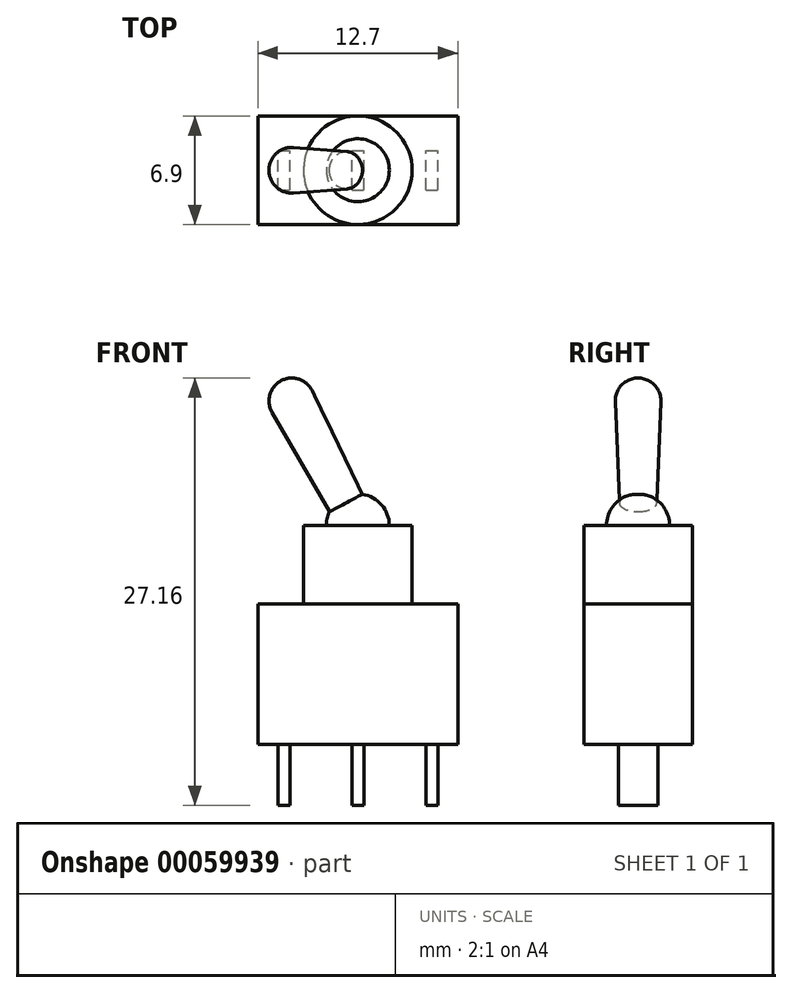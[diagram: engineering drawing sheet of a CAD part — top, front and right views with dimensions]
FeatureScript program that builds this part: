
annotation { "Feature Type Name" : "Feature", "Feature Type Description" : "" }
export const myFeature = defineFeature(function(context is Context, id is Id, definition is map)
    precondition{}
    {
        {
            var Q0;
            Q0=qCreatedBy(makeId("Top.planeOp"),FACE);
            var sketch = newSketch(context, id + "F0", { "sketchPlane" : qUnion([Q0])});
            skLineSegment(sketch, "E0.bottom", {"start": v(0, -3.45) * mm, "end": v(12.7, -3.45) * mm});
            skLineSegment(sketch, "E0.top", {"start": v(0, 3.45) * mm, "end": v(12.7, 3.45) * mm});
            skLineSegment(sketch, "E0.left", {"start": v(0, -3.45) * mm, "end": v(0, 3.45) * mm});
            skLineSegment(sketch, "E0.right", {"start": v(12.7, -3.45) * mm, "end": v(12.7, 3.45) * mm});
            skSolve(sketch);
        }
        {
            var Q0;
            Q0=makeQuery(id+"F0.imprint","IMPRINT",FACE,{"disambiguationData":[TD([[makeQuery(id+"F0.imprint","IMPRINT",EDGE,{"derivedFrom":sQuery(id+"F0.wireOp",EDGE,"E0.bottom")}),1.0]])]});
            extrude(context, id + "F1", {"entities" : qUnion([Q0]), "depth" : 8.9 * mm});
        }
        {
            var Q0;
            Q0=makeQuery(id+"F1.opExtrude","CAP_FACE",FACE,{"disambiguationData":[OSD([sQuery(id+"F0.wireOp",EDGE,"E0.bottom"),sQuery(id+"F0.wireOp",EDGE,"E0.top"),sQuery(id+"F0.wireOp",EDGE,"E0.left"),sQuery(id+"F0.wireOp",EDGE,"E0.right")])],"isStart":false});
            var sketch = newSketch(context, id + "F2", { "sketchPlane" : qUnion([Q0])});
            skCircle(sketch, "E1", {"center": v(6.35, 0) * mm, "radius": 3.45 * mm});
            skLineSegment(sketch, "E2", {"start": v(0, 0) * mm, "end": v(6.35, 0) * mm, "construction": true});
            skLineSegment(sketch, "E3", {"start": v(6.35, -3.45) * mm, "end": v(6.35, 3.45) * mm, "construction": true});
            skSolve(sketch);
        }
        {
            var Q0;
            Q0=makeQuery(id+"F2.imprint","IMPRINT",FACE,{"disambiguationData":[TD([[makeQuery(id+"F2.imprint","IMPRINT",EDGE,{"derivedFrom":sQuery(id+"F2.wireOp",EDGE,"E1")}),1.0]])]});
            extrude(context, id + "F3", {"entities" : qUnion([Q0]), "operationType" : NewBodyOperationType.ADD, "depth" : 5 * mm});
        }
        {
            var Q0;
            Q0=qCreatedBy(makeId("Front.planeOp"),FACE);
            var sketch = newSketch(context, id + "F4", { "sketchPlane" : qUnion([Q0])});
            skLineSegment(sketch, "E4", {"start": v(5.05, 13.9) * mm, "end": v(0.9, 21.08) * mm});
            skLineSegment(sketch, "E5", {"start": v(1.48, 23.09) * mm, "end": v(6.35, 13.9) * mm});
            skArc(sketch, "E6", {"start": v(1.48, 23.09) * mm, "mid": v(0.77, 22.2) * mm, "end": v(0.9, 21.08) * mm});
            skLineSegment(sketch, "E7", {"start": v(5.05, 13.9) * mm, "end": v(6.35, 13.9) * mm});
            skLineSegment(sketch, "E8", {"start": v(5.05, 13.9) * mm, "end": v(20.9, -13.56) * mm, "construction": true});
            skLineSegment(sketch, "E9", {"start": v(20.9, -13.56) * mm, "end": v(6.35, 13.9) * mm, "construction": true});
            skSolve(sketch);
        }
        {
            var Q0;
            Q0=makeQuery(id+"F4.imprint","IMPRINT",FACE,{"disambiguationData":[TD([[makeQuery(id+"F4.imprint","IMPRINT",EDGE,{"derivedFrom":sQuery(id+"F4.wireOp",EDGE,"E4")}),-1.0]])]});
            var Q1;
            Q1=sQuery(id+"F4.wireOp",EDGE,"E5");
            revolve(context, id + "F5", {"operationType" : NewBodyOperationType.ADD, "entities" : qUnion([Q0]), "axis" : qUnion([Q1]), "revolveType" : RevolveType.FULL});
        }
        {
            var Q0;
            Q0=qCreatedBy(makeId("Front.planeOp"),FACE);
            var sketch = newSketch(context, id + "F6", { "sketchPlane" : qUnion([Q0])});
            skLineSegment(sketch, "E10", {"start": v(4.35, 13.9) * mm, "end": v(8.35, 13.9) * mm});
            skArc(sketch, "E11", {"start": v(8.35, 13.9) * mm, "mid": v(6.35, 15.9) * mm, "end": v(4.35, 13.9) * mm});
            skSolve(sketch);
        }
        {
            var Q0;
            Q0 = qSketchRegion(id + "F6", true);
            var Q1;
            Q1=sQuery(id+"F6.wireOp",EDGE,"E10");
            revolve(context, id + "F7", {"operationType" : NewBodyOperationType.ADD, "entities" : qUnion([Q0]), "axis" : qUnion([Q1]), "revolveType" : RevolveType.FULL});
        }
        {
            var Q0;
            Q0=qCreatedBy(makeId("Top.planeOp"),FACE);
            var sketch = newSketch(context, id + "F8", { "sketchPlane" : qUnion([Q0])});
            skLineSegment(sketch, "E12.bottom", {"start": v(1.27, -1.25) * mm, "end": v(2.03, -1.25) * mm});
            skLineSegment(sketch, "E12.top", {"start": v(1.27, 1.25) * mm, "end": v(2.03, 1.25) * mm});
            skLineSegment(sketch, "E12.left", {"start": v(1.27, -1.25) * mm, "end": v(1.27, 1.25) * mm});
            skLineSegment(sketch, "E12.right", {"start": v(2.03, -1.25) * mm, "end": v(2.03, 1.25) * mm});
            skLineSegment(sketch, "E13.bottom", {"start": v(5.97, -1.25) * mm, "end": v(6.73, -1.25) * mm});
            skLineSegment(sketch, "E13.top", {"start": v(5.97, 1.25) * mm, "end": v(6.73, 1.25) * mm});
            skLineSegment(sketch, "E13.left", {"start": v(5.97, -1.25) * mm, "end": v(5.97, 1.25) * mm});
            skLineSegment(sketch, "E13.right", {"start": v(6.73, -1.25) * mm, "end": v(6.73, 1.25) * mm});
            skLineSegment(sketch, "E14.bottom", {"start": v(10.67, -1.25) * mm, "end": v(11.43, -1.25) * mm});
            skLineSegment(sketch, "E14.top", {"start": v(10.67, 1.25) * mm, "end": v(11.43, 1.25) * mm});
            skLineSegment(sketch, "E14.left", {"start": v(10.67, -1.25) * mm, "end": v(10.67, 1.25) * mm});
            skLineSegment(sketch, "E14.right", {"start": v(11.43, -1.25) * mm, "end": v(11.43, 1.25) * mm});
            skLineSegment(sketch, "E15", {"start": v(0, 0) * mm, "end": v(1.27, 0) * mm, "construction": true});
            skLineSegment(sketch, "E16", {"start": v(2.03, 0) * mm, "end": v(5.97, 0) * mm, "construction": true});
            skLineSegment(sketch, "E17", {"start": v(6.73, 0) * mm, "end": v(10.67, 0) * mm, "construction": true});
            skLineSegment(sketch, "E18", {"start": v(11.43, 0) * mm, "end": v(12.7, 0) * mm, "construction": true});
            skLineSegment(sketch, "E19", {"start": v(1.65, 1.25) * mm, "end": v(1.65, 3.45) * mm, "construction": true});
            skLineSegment(sketch, "E20", {"start": v(6.35, 1.25) * mm, "end": v(6.35, 3.45) * mm, "construction": true});
            skSolve(sketch);
        }
        {
            var Q0;
            Q0 = qSketchRegion(id + "F8", true);
            extrude(context, id + "F9", {"entities" : qUnion([Q0]), "operationType" : NewBodyOperationType.ADD, "oppositeDirection" : true, "depth" : 3.9 * mm});
        }
    });
